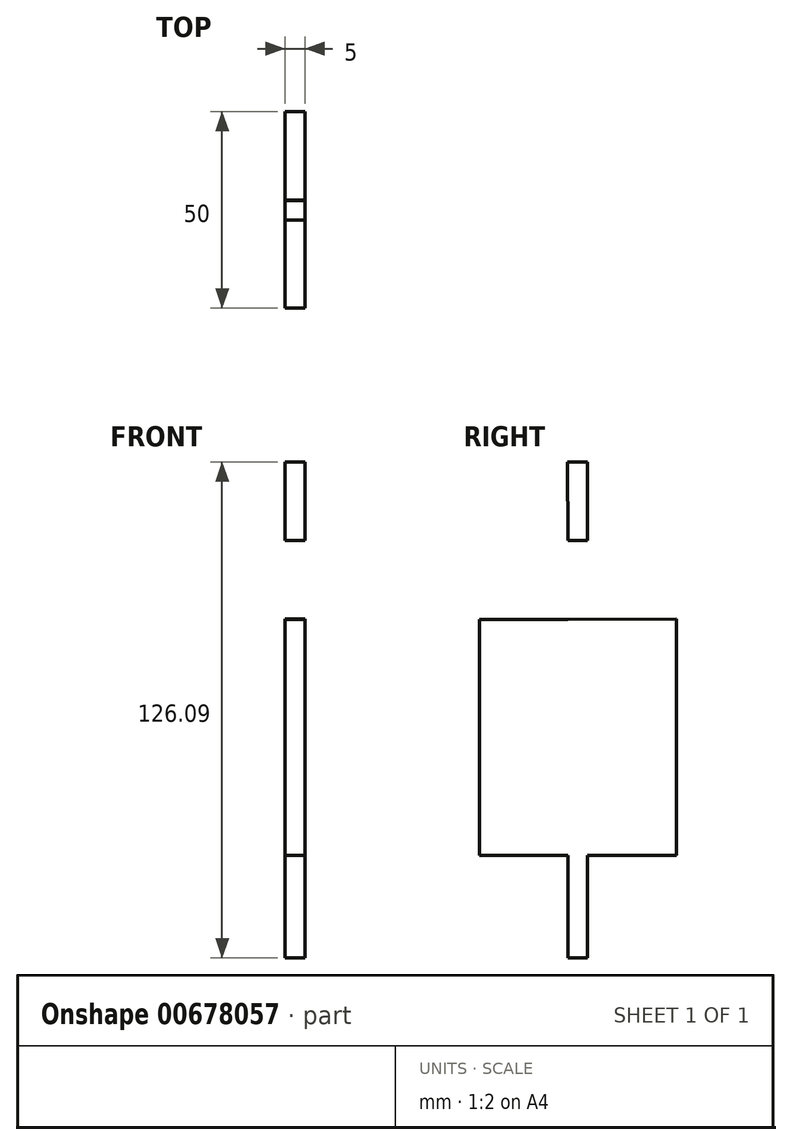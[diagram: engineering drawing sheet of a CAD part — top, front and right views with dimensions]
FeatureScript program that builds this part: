
annotation { "Feature Type Name" : "Feature", "Feature Type Description" : "" }
export const myFeature = defineFeature(function(context is Context, id is Id, definition is map)
    precondition{}
    {
        {
            var Q0;
            Q0=qCreatedBy(makeId("Right.planeOp"),FACE);
            var sketch = newSketch(context, id + "F0", { "sketchPlane" : qUnion([Q0])});
            skLineSegment(sketch, "E0", {"start": v(0, 0) * mm, "end": v(0, -60) * mm});
            skLineSegment(sketch, "E1", {"start": v(0, -60) * mm, "end": v(12.4, -60) * mm});
            skLineSegment(sketch, "E2.0", {"start": v(27.5, -60) * mm, "end": v(27.5, -81.07) * mm});
            skLineSegment(sketch, "E3", {"start": v(12, -60) * mm, "end": v(12.4, -60) * mm});
            skLineSegment(sketch, "E4", {"start": v(0, -60) * mm, "end": v(12, -60) * mm});
            skLineSegment(sketch, "E5", {"start": v(22.5, -86.09) * mm, "end": v(22.5, -60) * mm});
            skPoint(sketch, "E6.trimOffspring.start.orphan", {"position": v(25, -60) * mm});
            skLineSegment(sketch, "E7", {"start": v(27.5, -81.07) * mm, "end": v(27.5, -86.09) * mm});
            skLineSegment(sketch, "E8", {"start": v(22.5, -86.09) * mm, "end": v(27.5, -86.09) * mm});
            skLineSegment(sketch, "E9", {"start": v(11.37, -27.14) * mm, "end": v(11.37, -26.74) * mm});
            skLineSegment(sketch, "E10", {"start": v(38.63, -27.14) * mm, "end": v(38.63, -26.74) * mm});
            skLineSegment(sketch, "E11", {"start": v(0, -60) * mm, "end": v(22.5, -60) * mm});
            skLineSegment(sketch, "E12.trimOffspring", {"start": v(22.5, -60) * mm, "end": v(0, -60) * mm});
            skLineSegment(sketch, "E13", {"start": v(22.5, -0.06) * mm, "end": v(0, 0) * mm});
            skLineSegment(sketch, "E14.0", {"start": v(50, 0.01) * mm, "end": v(50, -60) * mm});
            skLineSegment(sketch, "E15", {"start": v(50, 0.01) * mm, "end": v(22.5, -0.06) * mm});
            skLineSegment(sketch, "E16", {"start": v(50, -60) * mm, "end": v(27.5, -60) * mm});
            skLineSegment(sketch, "E17", {"start": v(22.45, 19.94) * mm, "end": v(22.4, 40) * mm});
            skLineSegment(sketch, "E18", {"start": v(22.4, 40) * mm, "end": v(27.4, 40) * mm});
            skLineSegment(sketch, "E19", {"start": v(27.4, 40) * mm, "end": v(27.45, 19.96) * mm});
            skLineSegment(sketch, "E20.0", {"start": v(27.45, 19.96) * mm, "end": v(22.45, 19.94) * mm});
            skPoint(sketch, "E21.orphan", {"position": v(27.5, 0) * mm});
            skSolve(sketch);
        }
        {
            var Q0;
            {var subQ1=sQuery(id+"F0.wireOp",EDGE,"E0");Q0=makeQuery(id+"F0.imprint","IMPRINT",FACE,{"disambiguationData":[TD([[makeQuery(id+"F0.imprint","IMPRINT",EDGE,{"derivedFrom":subQ1}),1.0]])]});}
            var Q1;
            Q1=makeQuery(id+"F0.imprint","IMPRINT",FACE,{"disambiguationData":[TD([[makeQuery(id+"F0.imprint","IMPRINT",EDGE,{"derivedFrom":sQuery(id+"F0.wireOp",EDGE,"E17")}),-1.0]])]});
            extrude(context, id + "F1", {"entities" : qUnion([Q0, Q1]), "depth" : 5 * mm, "offsetDistance" : 25 * mm});
        }
    });
